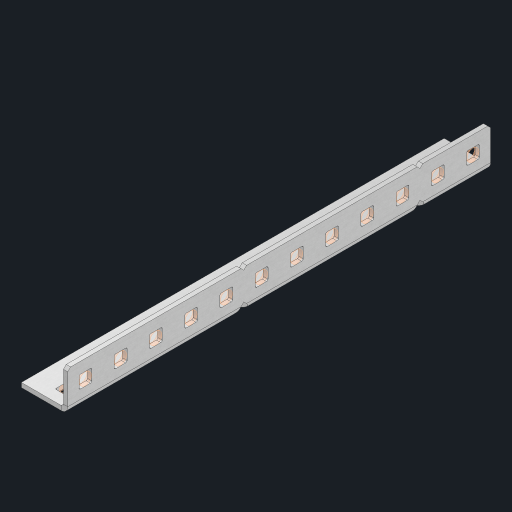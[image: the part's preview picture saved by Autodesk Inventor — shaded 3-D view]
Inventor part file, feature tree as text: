
AUTODESK INVENTOR PART (.ipt)
format: ipt  version: 2023 (Build 270158000, 158)  size: 626,688 bytes
history: native  units: in
note: dims shown in document units (in); Inventor stores cm internally (conversion verified against a paired STEP export)
features: other x29, extrude x23, sheet_metal_op x10, sketch x8, mirror x1, pattern_linear x1, chamfer x1
ambient origin geometry x8: Origin, YZ Plane, XZ Plane, XY Plane, X Axis, Y Axis, Z Axis, Center Point
bodies: Solid1 (feature_tree), Body (feature_tree)
feature tree (73):
  other  "Flange Pattern Plane"
  sheet_metal_op  "Flange Pattern"
  sheet_metal_op  "Body Pattern"
  other  "Arc Length"
  mirror  "Notch Mirror"
  pattern_linear  "Notch Pattern"  Spacing1=0.25in  [1 undecoded]
  chamfer  "End Chamfer"
  extrude  "Half Cut"  Depth=0.0625in
  sketch  "Sketch1"  dims[d0=1.5in]
  other  "Plate1"
  sketch  "Sketch2"  dims[d1=6.0in]
  other  "Plate2"
  sheet_metal_op  "Bend1"
  sheet_metal_op  "Corner1"
  sketch  "Sketch3"  dims[d2=0.0625in]
  other  "Flange Pattern Sketch"
  sketch  "Sketch7"  dims[d3=0.0625in]
  other  "Srf1"
  other  "Srf2"
  sketch  "Sketch8"  dims[d4=0.0312in]
  sketch  "Sketch9"  dims[d5=0.125in]
  other  "Srf91"
  sheet_metal_op  "Body Pattern Sketch"
  other  "Srf92"
  sketch  "Sketch13"  dims[d6=0.0625in]
  sketch  "Sketch14"  dims[d7=0.5in d8=90.0deg d9=0.0312in d10=0.25in d11=0.0625in d12=0.0625in d16=0.182in d17=0.02in d18=0.0625in d19=0.0in d20=0.25in d21=0.25in d46=0.172in d47=1.0in d48=0.0in d49=0.182in d50=0.02in d51=0.25in d52=0.25in d53=0.0625in d54=0.0in d55=0.172in d56=1.0in d57=0.0in d60=4.7244in d62=0.5in d63=0.3937in d65=0.5in d85=0.1473in d86=0.1782in d88=0.04in d89=0.0625in d90=0.0in d91=0.04in d92=0.0491in d95=2.5in d96=0.04in d97=0.25in d98=45.0deg d101=0.0in d102=2.497in d131=0.5in d132=4.7244in d134=0.5in d139=0.5in]
  other  "Srf856"
  other  "Srf1310"
  other  "Srf1311"
  other  "Srf1312"
  other  "Srf1376"
  other  "Srf1377"
  other  "Srf1728"
  other  "Srf1755"
  other  "Srf1878"
  other  "Srf1879"
  other  "Srf1880"
  other  "Srf1881"
  other  "Srf1882"
  other  "Srf1883"
  other  "Srf1942"
  other  "Srf1943"
  other  "Srf1944"
  other  "Srf1945"
  other  "Srf1946"
  other  "Srf1947"
  sheet_metal_op  "Flange Stamp"
  sheet_metal_op  "Flange Circle"
  sheet_metal_op  "Body Stamp"
  sheet_metal_op  "Body Circle"
  sheet_metal_op  "Notch"
  extrude  "ExtrusionSrf2"  Depth=0.0625in
  extrude  "ExtrusionSrf92"  Depth=0.5in
  extrude  "ExtrusionSrf856"  Depth=0.02in
  extrude  "ExtrusionSrf1310"  Depth=0.0625in
  extrude  "ExtrusionSrf1311"  TaperAngle=0.0deg  [1 undecoded]
  extrude  "ExtrusionSrf1312"  Depth=0.5in
  extrude  "ExtrusionSrf1376"  Depth=0.5in
  extrude  "ExtrusionSrf1377"  Depth=0.5in
  extrude  "ExtrusionSrf1728"  Depth=0.5in TaperAngle=0.0deg
  extrude  "ExtrusionSrf1755"  Depth=0.5in
  extrude  "ExtrusionSrf1878"  Depth=0.02in
  extrude  "ExtrusionSrf1879"  Depth=0.5in
  extrude  "ExtrusionSrf1880"  Depth=0.5in
  extrude  "ExtrusionSrf1881"  Depth=0.0625in
  extrude  "ExtrusionSrf1882"  TaperAngle=0.0deg  [1 undecoded]
  extrude  "ExtrusionSrf1883"  Depth=0.5in
  extrude  "ExtrusionSrf1942"  Depth=0.5in TaperAngle=0.0deg
  extrude  "ExtrusionSrf1943"  Depth=0.5in
  extrude  "ExtrusionSrf1944"  Depth=0.5in
  extrude  "ExtrusionSrf1945"  Depth=0.5in
  extrude  "ExtrusionSrf1946"  Depth=0.5in
  extrude  "ExtrusionSrf1947"  Depth=0.5in
note: 3 required parameter values undecoded (feature->parameter linkage not recoverable at this tier; creation-order binding heuristic only, values carry confidence <= 0.55)
